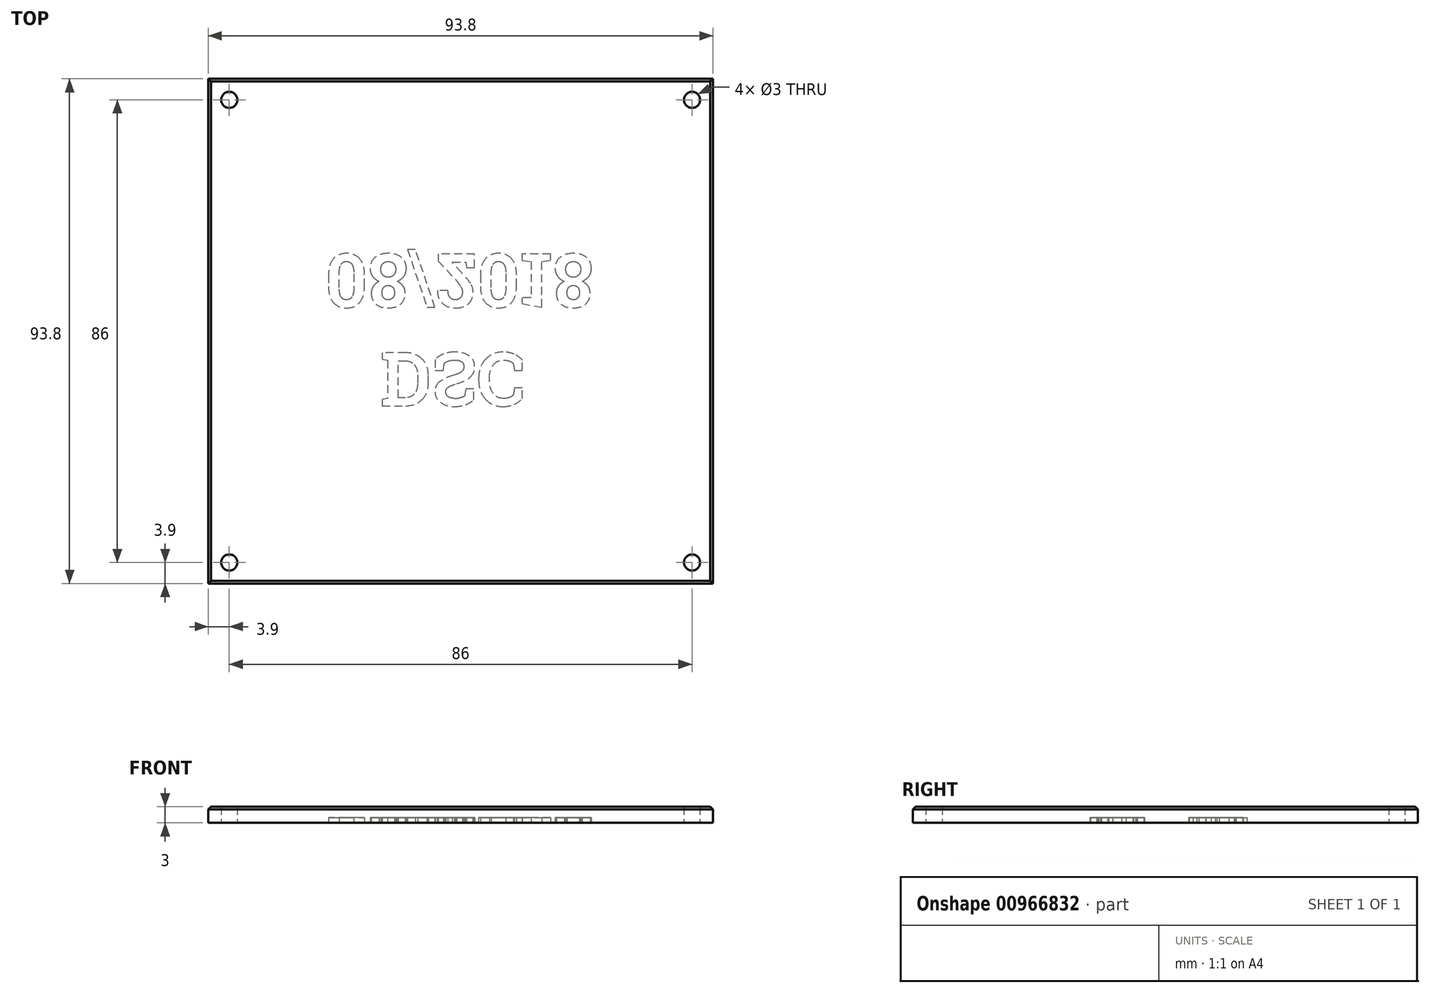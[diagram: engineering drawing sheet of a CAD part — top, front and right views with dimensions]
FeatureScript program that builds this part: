
annotation { "Feature Type Name" : "Feature", "Feature Type Description" : "" }
export const myFeature = defineFeature(function(context is Context, id is Id, definition is map)
    precondition{}
    {
        {
            var Q0;
            Q0=qCreatedBy(makeId("Top.planeOp"),FACE);
            var sketch = newSketch(context, id + "F0", { "sketchPlane" : qUnion([Q0])});
            skLineSegment(sketch, "E0.bottom", {"start": v(-46.9, 46.9) * mm, "end": v(46.9, 46.9) * mm});
            skLineSegment(sketch, "E0.top", {"start": v(-46.9, -46.9) * mm, "end": v(46.9, -46.9) * mm});
            skLineSegment(sketch, "E0.left", {"start": v(-46.9, 46.9) * mm, "end": v(-46.9, -46.9) * mm});
            skLineSegment(sketch, "E0.right", {"start": v(46.9, 46.9) * mm, "end": v(46.9, -46.9) * mm});
            skSolve(sketch);
        }
        {
            var Q0;
            Q0 = qSketchRegion(id + "F0", true);
            extrude(context, id + "F1", {"entities" : qUnion([Q0]), "depth" : 3 * mm, "offsetDistance" : 25 * mm});
        }
        {
            var Q0;
            Q0=makeQuery(id+"F1.opExtrude","CAP_FACE",FACE,{"disambiguationData":[OSD([sQuery(id+"F0.wireOp",EDGE,"E0.bottom"),sQuery(id+"F0.wireOp",EDGE,"E0.top"),sQuery(id+"F0.wireOp",EDGE,"E0.left"),sQuery(id+"F0.wireOp",EDGE,"E0.right")])],"isStart":true});
            var sketch = newSketch(context, id + "F2", { "sketchPlane" : qUnion([Q0])});
            skLineSegment(sketch, "E1.bottom", {"start": v(-43, 43) * mm, "end": v(43, 43) * mm, "construction": true});
            skLineSegment(sketch, "E1.top", {"start": v(-43, -43) * mm, "end": v(43, -43) * mm, "construction": true});
            skLineSegment(sketch, "E1.left", {"start": v(-43, 43) * mm, "end": v(-43, -43) * mm, "construction": true});
            skLineSegment(sketch, "E1.right", {"start": v(43, 43) * mm, "end": v(43, -43) * mm, "construction": true});
            skPoint(sketch, "E2", {"position": v(-43, 43) * mm});
            skPoint(sketch, "E3", {"position": v(43, 43) * mm});
            skPoint(sketch, "E4", {"position": v(43, -43) * mm});
            skPoint(sketch, "E5", {"position": v(-43, -43) * mm});
            skSolve(sketch);
        }
        {
            var Q0;
            Q0=makeQuery(id+"F1.opExtrude","CAP_EDGE",EDGE,{"disambiguationData":[OSD([sQuery(id+"F0.wireOp",EDGE,"E0.left")])],"isStart":false});
            var Q1;
            Q1=makeQuery(id+"F1.opExtrude","CAP_EDGE",EDGE,{"disambiguationData":[OSD([sQuery(id+"F0.wireOp",EDGE,"E0.bottom")])],"isStart":false});
            var Q2;
            Q2=makeQuery(id+"F1.opExtrude","CAP_EDGE",EDGE,{"disambiguationData":[OSD([sQuery(id+"F0.wireOp",EDGE,"E0.top")])],"isStart":false});
            var Q3;
            Q3=makeQuery(id+"F1.opExtrude","CAP_EDGE",EDGE,{"disambiguationData":[OSD([sQuery(id+"F0.wireOp",EDGE,"E0.right")])],"isStart":false});
            chamfer(context, id + "F3", {"entities" : qUnion([Q0, Q1, Q2, Q3]), "width" : 0.5 * mm, "tangentPropagation" : true});
        }
        {
            var Q0;
            Q0=sQuery(id+"F2.wireOp",VERTEX,"E2");
            var Q1;
            Q1=sQuery(id+"F2.wireOp",VERTEX,"E3");
            var Q2;
            Q2=sQuery(id+"F2.wireOp",VERTEX,"E5");
            var Q3;
            Q3=sQuery(id+"F2.wireOp",VERTEX,"E4");
            var Q4;
            Q4=makeQuery(id+"F1.opExtrude","SWEPT_BODY",BODY,{"disambiguationData":[OSD([sQuery(id+"F0.wireOp",EDGE,"E0.bottom"),sQuery(id+"F0.wireOp",EDGE,"E0.top"),sQuery(id+"F0.wireOp",EDGE,"E0.left"),sQuery(id+"F0.wireOp",EDGE,"E0.right")])]});
            hole(context, id + "F4", {"style" : HoleStyle.SIMPLE, "endStyle" : HoleEndStyle.THROUGH, "holeDiameter" : 3 * mm, "majorDiameter" : 5 * mm, "isTappedThrough" : true, "tappedDepth" : 12 * mm, "tapClearance" : 3, "startFromSketch" : true, "locations" : qUnion([Q0, Q1, Q2, Q3]), "scope" : qUnion([Q4])});
        }
        {
            var Q0;
            Q0=makeQuery(id+"F1.opExtrude","CAP_FACE",FACE,{"disambiguationData":[OSD([sQuery(id+"F0.wireOp",EDGE,"E0.bottom"),sQuery(id+"F0.wireOp",EDGE,"E0.top"),sQuery(id+"F0.wireOp",EDGE,"E0.left"),sQuery(id+"F0.wireOp",EDGE,"E0.right")])],"isStart":true});
            var sketch = newSketch(context, id + "F5", { "sketchPlane" : qUnion([Q0])});
            skText(sketch, "E6", { "text": "   DSC\n08/2018", "fontName": "RobotoSlab-Bold.ttf"});
            const initialGuessF5  = {"E6": [-0.02521, 0.00401, 1, 0, 0.01]};
            skSetInitialGuess(sketch, initialGuessF5);
            skSolve(sketch);
        }
        {
            var Q0;
            Q0 = qSketchRegion(id + "F5", true);
            extrude(context, id + "F6", {"entities" : qUnion([Q0]), "operationType" : NewBodyOperationType.REMOVE, "oppositeDirection" : true, "depth" : 1 * mm, "offsetDistance" : 25 * mm});
        }
    });
